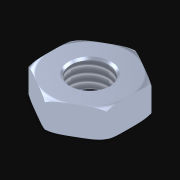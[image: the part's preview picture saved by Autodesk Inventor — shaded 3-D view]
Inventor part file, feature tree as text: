
AUTODESK INVENTOR PART (.ipt)
format: ipt  version: 2021 (Build 250183000, 183)  size: 166,400 bytes
history: native  units: in
note: dims shown in document units (in); Inventor stores cm internally (conversion verified against a paired STEP export)
features: other x1, imported_body x1, thread x1
ambient origin geometry x8: Origin, YZ Plane, XZ Plane, XY Plane, X Axis, Y Axis, Z Axis, Center Point
bodies: Body1 (feature_tree)
feature tree (3):
  parser-record x1  (decoder bookkeeping rows leaked as tree rows — omitted from the tree; the rows remain in map.json)
  imported_body  "Base1"
  thread  "Thread1"  [1 undecoded]
note: 1 required parameter value undecoded (feature->parameter linkage not recoverable at this tier; creation-order binding heuristic only, values carry confidence <= 0.55)
